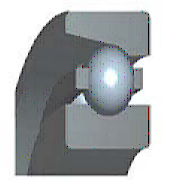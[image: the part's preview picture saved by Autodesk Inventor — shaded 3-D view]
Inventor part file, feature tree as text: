
AUTODESK INVENTOR PART (.ipt)
format: ipt  version: 2019.2 (Build 232265000, 265)  size: 371,712 bytes
history: native  units: mm
features: sketch x2
ambient origin geometry x8: Origin, YZ Plane, XZ Plane, XY Plane, X Axis, Y Axis, Z Axis, Center Point
bodies: Solid1 (feature_tree)
feature tree (2):
  sketch  "Sketch1"  dims[d1=30.0mm]
  sketch  "Sketch2"  dims[d2=7.2mm d3=10.0mm d5=15.0deg d8=5.2mm d20=1.745329mm d24=8.55mm d35=0.6mm d36=0.3mm d37=0.3mm d38=16.52mm d39=23.48mm d40=17.912mm d41=0.6mm d42=9.0mm d43=5.2mm d44=15.0deg d46=90.0deg d47=90.0deg d48=60.0mm d49=360.0deg d51=0.0mm d52=0.0mm d53=0.0mm d54=0.0mm d55=0.0mm]
